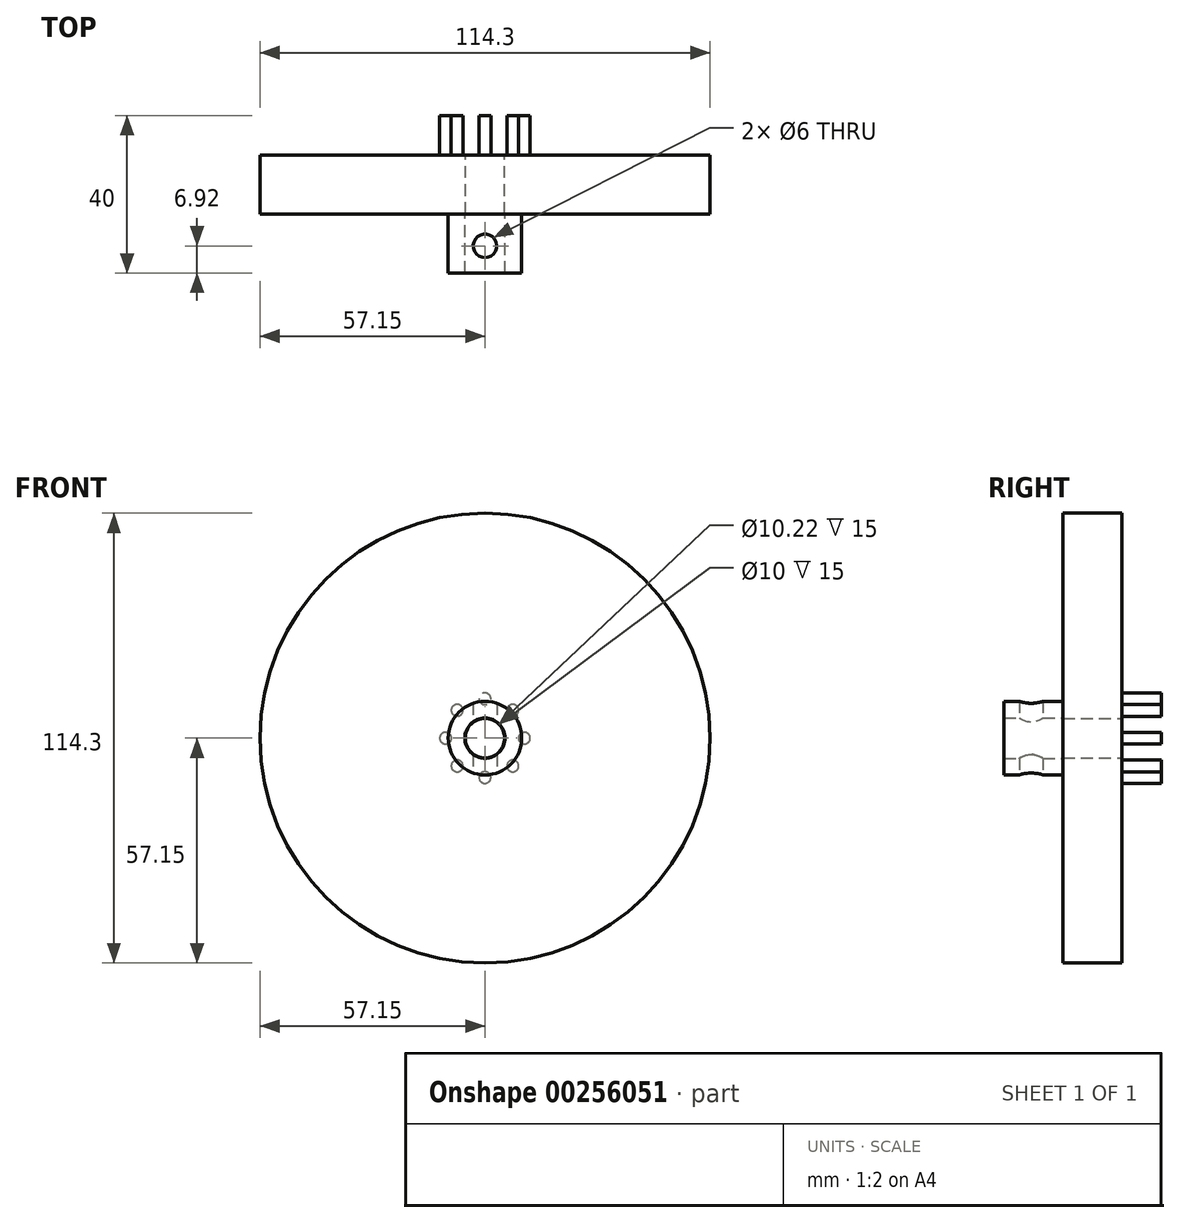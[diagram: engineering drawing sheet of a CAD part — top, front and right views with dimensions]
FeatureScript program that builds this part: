
annotation { "Feature Type Name" : "Feature", "Feature Type Description" : "" }
export const myFeature = defineFeature(function(context is Context, id is Id, definition is map)
    precondition{}
    {
        {
            var Q0;
            Q0=qCreatedBy(makeId("Front.planeOp"),FACE);
            var sketch = newSketch(context, id + "F0", { "sketchPlane" : qUnion([Q0])});
            skCircle(sketch, "E0", {"center": v(0, 0) * mm, "radius": 5 * mm});
            skCircle(sketch, "E1", {"center": v(0, 0) * mm, "radius": 57.15 * mm});
            skSolve(sketch);
        }
        {
            var Q0;
            Q0 = qSketchRegion(id + "F0", true);
            extrude(context, id + "F1", {"entities" : qUnion([Q0]), "depth" : 15 * mm});
        }
        {
            var Q0;
            Q0=makeQuery(id+"F1.opExtrude","CAP_FACE",FACE,{"disambiguationData":[OSD([sQuery(id+"F0.wireOp",EDGE,"E0"),sQuery(id+"F0.wireOp",EDGE,"E1")])],"isStart":false});
            var sketch = newSketch(context, id + "F2", { "sketchPlane" : qUnion([Q0])});
            skCircle(sketch, "E2", {"center": v(0, 0) * mm, "radius": 9.35 * mm});
            skCircle(sketch, "E3", {"center": v(0, 0) * mm, "radius": 5.1 * mm});
            skSolve(sketch);
        }
        {
            var Q0;
            Q0 = qSketchRegion(id + "F2", true);
            extrude(context, id + "F3", {"entities" : qUnion([Q0]), "operationType" : NewBodyOperationType.ADD, "depth" : 15 * mm});
        }
        {
            var Q0;
            Q0=qCreatedBy(makeId("Top.planeOp"),FACE);
            var sketch = newSketch(context, id + "F4", { "sketchPlane" : qUnion([Q0])});
            skCircle(sketch, "E4", {"center": v(0, -23.08) * mm, "radius": 3 * mm});
            skSolve(sketch);
        }
        {
            var Q0;
            Q0 = qSketchRegion(id + "F4", true);
            extrude(context, id + "F5", {"entities" : qUnion([Q0]), "operationType" : NewBodyOperationType.REMOVE, "endBound" : BoundingType.SYMMETRIC, "depth" : 25.4 * mm});
        }
        {
            var Q0;
            Q0=makeQuery(id+"F1.opExtrude","CAP_FACE",FACE,{"disambiguationData":[OSD([sQuery(id+"F0.wireOp",EDGE,"E0"),sQuery(id+"F0.wireOp",EDGE,"E1")])],"isStart":true});
            var sketch = newSketch(context, id + "F6", { "sketchPlane" : qUnion([Q0])});
            skCircle(sketch, "E5", {"center": v(0, 10) * mm, "radius": 1.5 * mm});
            skCircle(sketch, "E6", {"center": v(7.07, 7.07) * mm, "radius": 1.5 * mm});
            skCircle(sketch, "E7", {"center": v(10, 0) * mm, "radius": 1.5 * mm});
            skCircle(sketch, "E8", {"center": v(7.07, -7.07) * mm, "radius": 1.5 * mm});
            skCircle(sketch, "E9", {"center": v(0, -10) * mm, "radius": 1.5 * mm});
            skCircle(sketch, "E10", {"center": v(-10, 0) * mm, "radius": 1.5 * mm});
            skCircle(sketch, "E11", {"center": v(-7.07, -7.07) * mm, "radius": 1.5 * mm});
            skCircle(sketch, "E12", {"center": v(-7.07, 7.07) * mm, "radius": 1.5 * mm});
            skSolve(sketch);
        }
        {
            var Q0;
            Q0 = qSketchRegion(id + "F6", true);
            extrude(context, id + "F7", {"entities" : qUnion([Q0]), "operationType" : NewBodyOperationType.ADD, "depth" : 10 * mm});
        }
    });
